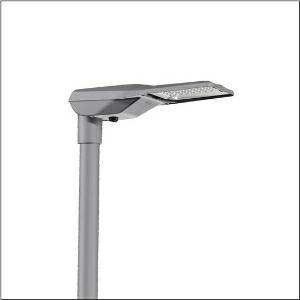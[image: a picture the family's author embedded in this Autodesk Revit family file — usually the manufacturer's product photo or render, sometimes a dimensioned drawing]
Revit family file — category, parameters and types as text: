
# Revit family: streetlight_sl_21_iq_mini___p0_8ab_5xe2r31u08jb_749f
name_source: partatom
category: Lighting Fixtures
units: mm (PartAtom-declared; Revit-internal decimal feet)

## family parameters
Cut with Voids When Loaded = No
Host = Face
Light Source = No
Part Type = Normal
Room Calculation Point = No
Round Connector Dimension = Use Diameter
Shared = No

## types (1)
- --- (1 x LED, 9740 lm, 72.5 W, 3000K)
    Apparent Load = 73 VA
    CIE Flux Codes = 39 72 97 100 100
    Color Rendering = 70
    Color Temperature = 3000K
    Default Elevation = 1800 mm
    Description = Streetlight SL 21 iQ mini, mast luminaire, primary light control with lens, of PMMA, primary optical cover: cover, of toughened safety glass, transparent, light distribution: P0.8aB, light emission: direct distribution, primary light characteristic: asymmetric, installation type: post-top, side-entry, LED, High Power LED, rated luminous flux: 9.740lm, luminous efficacy: 134lm/W, light colour: 730, colour temperature: 3000K, control gear: iQ-Street Remote, D4i with power reduction, control: pre-setting: logarithmic dimming characteristic, Street-Remote, Auto-Match, Temp-Guard, Lumen-Switch, Night-Set, Smart-Wire, Light-Fading, Desk-Remote (wireless, voltage-free reading and setting of iQ features in the workshop via application-optimized NFC function/RFID function), optimised constant luminous flux control (CLO 2.0), mains connection: 220..240V, AC, 50/60Hz, start of lifetime: 73W, end of service life: 76W, reduction: 33W, luminaire housing, of diecast aluminium, powder-coated, SITECO metallic grey (DB 702S), corrosivity category C5 high according to DIN EN ISO 12944, please order mast flange separately, inclination adjustable: 0°, 5°, 10°, 15°, sealing non-destructively replaceable, multi-level sealing system, length: 628mm, width: 235mm, height: 110mm, mast flange for spigot size: 42mm (side-entry): 5XC10008XM4, 60/48mm (side-entry/post-top): 5XC10108XM2, 76/60mm (side-entry/post-top): 5XC10108XM1, mounting height: 4..8m, Smart Interface below, protection rating (complete): IP66, insulation class (complete): insulation class II (safety insulation), certification: CE, ENEC, ENEC+, VDE, impact resistance: IK10, permissible operating ambient temperature for outdoor applications: -40..+50°C, standard-compliant lighting for roads and squares, packaging unit: 1 piece

Light Distribution: P0.8aB
    Height = 110 mm
    Lamp = 1 x LED
    Lamp Light Flux = 9740 lm
    Lamp Power = 72.5 W
    Lamp count = 1
    Length = 625 mm
    Luminous efficacy = 134 lm/W
    Manufacturer = Siteco
    ModVariant = No
    Model = 5XE2R31U08JB
    Number of Poles = 1
    OnlyDefault = Yes
    Power Factor = 1
    Product Name = Streetlight SL 21 iQ mini | P0.8aB
    Product group = mast luminaire | pylon top
    ProductGroupID = 6100
    Protection Class = Protection class II
    Protection Degree = IP 66
    RLX_Detail_Level = 1
    RLX_Emergency_Light_Flux = 0 lm
    RLX_Emergency_Type = 0
    RLX_Emergency_Type_DB = No
    RlxData = <blob elided: 92045 chars, md5=5d9723ba>
    Socket = socket
    Standby Power = 0 W
    System Light Flux = 9740 lm
    System Power = 73 W
    Type Comments = factory setting: luminous flux: 100 % | dim-lin: 254 | 755 mA
    Type Image = l_1003516.jpg
    URL = http://relux.com
    VarID = @adj_079105
    Voltage = 0 V
    Weight = 0.00 kg
    Width = 234 mm

## geometry (parser evidence)
native form markers: Blend x4, Sweep x12
no freeform markers — native parametric forms only
